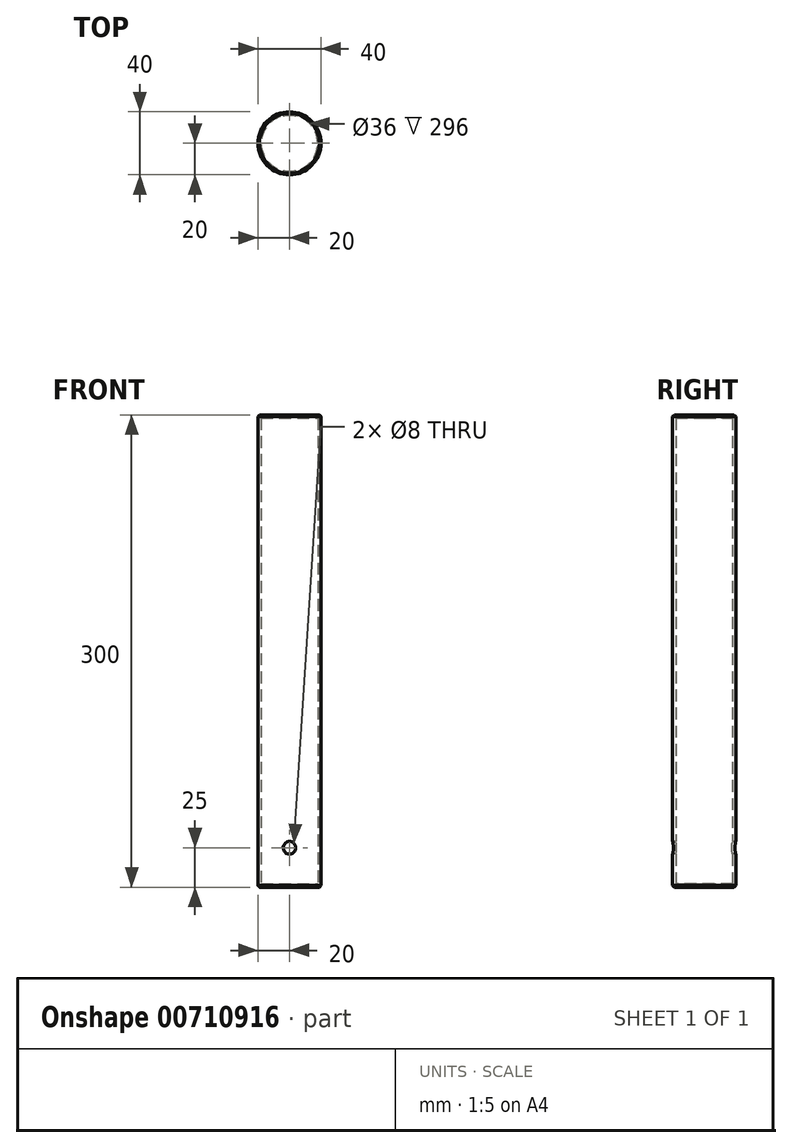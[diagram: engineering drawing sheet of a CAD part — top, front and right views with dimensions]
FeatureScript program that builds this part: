
annotation { "Feature Type Name" : "Feature", "Feature Type Description" : "" }
export const myFeature = defineFeature(function(context is Context, id is Id, definition is map)
    precondition{}
    {
        {
            var Q0;
            Q0=qCreatedBy(makeId("Front.planeOp"),FACE);
            var sketch = newSketch(context, id + "F0", { "sketchPlane" : qUnion([Q0])});
            skLineSegment(sketch, "E0", {"start": v(0, 0) * mm, "end": v(20, 0) * mm});
            skLineSegment(sketch, "E1", {"start": v(20, 0) * mm, "end": v(20, 300) * mm});
            skLineSegment(sketch, "E2", {"start": v(20, 300) * mm, "end": v(0, 300) * mm});
            skLineSegment(sketch, "E3", {"start": v(0, 300) * mm, "end": v(0, 298) * mm});
            skLineSegment(sketch, "E4", {"start": v(0, 298) * mm, "end": v(18, 298) * mm});
            skLineSegment(sketch, "E5", {"start": v(18, 298) * mm, "end": v(18, 2) * mm});
            skLineSegment(sketch, "E6", {"start": v(18, 2) * mm, "end": v(0, 2) * mm});
            skLineSegment(sketch, "E7", {"start": v(0, 2) * mm, "end": v(0, 0) * mm});
            skSolve(sketch);
        }
        {
            var Q0;
            Q0=makeQuery(id+"F0.imprint","IMPRINT",FACE,{"disambiguationData":[TD([[makeQuery(id+"F0.imprint","IMPRINT",EDGE,{"derivedFrom":sQuery(id+"F0.wireOp",EDGE,"E0")}),1.0]])]});
            var sketch = newSketch(context, id + "F1", { "sketchPlane" : qUnion([Q0])});
            skLineSegment(sketch, "E8", {"start": v(0, 0) * mm, "end": v(0, 304.67) * mm, "construction": true});
            skSolve(sketch);
        }
        {
            var Q0;
            Q0=makeQuery(id+"F0.imprint","IMPRINT",FACE,{"disambiguationData":[TD([[makeQuery(id+"F0.imprint","IMPRINT",EDGE,{"derivedFrom":sQuery(id+"F0.wireOp",EDGE,"E0")}),1.0]])]});
            var Q1;
            Q1=sQuery(id+"F1.wireOp",EDGE,"E8");
            revolve(context, id + "F2", {"entities" : qUnion([Q0]), "axis" : qUnion([Q1]), "revolveType" : RevolveType.FULL});
        }
        {
            var Q0;
            Q0=makeQuery(id+"F2.opRevolve","SWEPT_EDGE",EDGE,{"disambiguationData":[OSD([sQuery(id+"F0.wireOp",EDGE,"E1"),sQuery(id+"F0.wireOp",EDGE,"E2")])]});
            chamfer(context, id + "F3", {"entities" : qUnion([Q0]), "width" : 1 * mm, "tangentPropagation" : true});
        }
        {
            var Q0;
            Q0=makeQuery(id+"F2.opRevolve","SWEPT_EDGE",EDGE,{"disambiguationData":[OSD([sQuery(id+"F0.wireOp",EDGE,"E0"),sQuery(id+"F0.wireOp",EDGE,"E1")])]});
            chamfer(context, id + "F4", {"entities" : qUnion([Q0]), "width" : 1 * mm, "tangentPropagation" : true});
        }
        {
            var Q0;
            Q0=qCreatedBy(makeId("Front.planeOp"),FACE);
            cPlane(context, id + "F5", {"entities" : qUnion([Q0]), "cplaneType" : CPlaneType.OFFSET, "offset" : 20 * mm, "width" : 150 * mm, "height" : 150 * mm});
        }
        {
            var Q0;
            Q0=qCreatedBy(id+"F5.planeOp",FACE);
            var sketch = newSketch(context, id + "F6", { "sketchPlane" : qUnion([Q0])});
            skCircle(sketch, "E9", {"center": v(0, 25) * mm, "radius": 4 * mm});
            skSolve(sketch);
        }
        {
            var Q0;
            Q0 = qSketchRegion(id + "F6", true);
            extrude(context, id + "F7", {"entities" : qUnion([Q0]), "operationType" : NewBodyOperationType.REMOVE, "oppositeDirection" : true, "depth" : 40 * mm, "offsetDistance" : 25 * mm});
        }
    });
